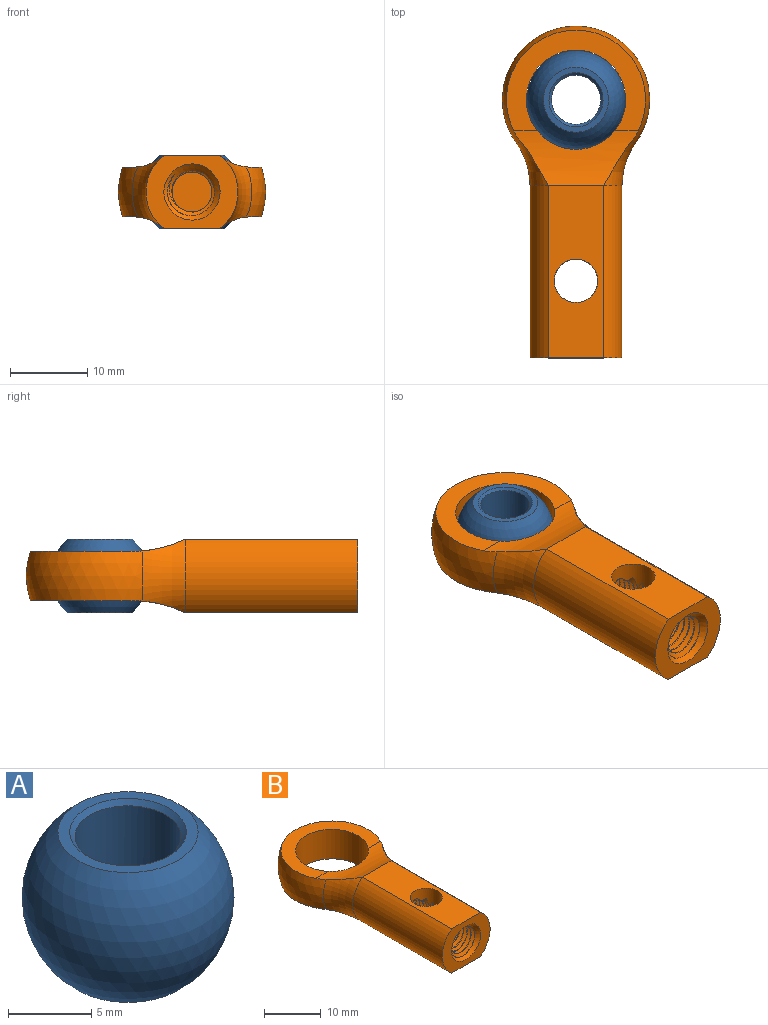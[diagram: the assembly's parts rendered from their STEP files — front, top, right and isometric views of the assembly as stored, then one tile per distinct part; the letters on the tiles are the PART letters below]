
ASSEMBLY  parts=2 mates=1
PART A: 6 faces, bbox 12.7x12.7x9.5 mm
  f0: cone r=3.49mm half-angle=45deg, axis (0,0,1), area 9.4mm2, adj f2,f4
  f1: cone r=3.49mm half-angle=45deg, axis (0,0,-1), area 9.4mm2, adj f2,f5
  f2: cylinder r=3.17mm len=8.89mm, axis (0,0,1), area 177.3mm2, adj f0,f1
  f3: sphere r=6.35mm, area 380mm2, adj f4,f5
  f4: plane 8.4x8.4mm, normal (0,0,1), area 17.1mm2, adj f0,f3
  f5: plane 8.4x8.4mm, normal (0,0,-1), area 17.1mm2, adj f1,f3
PART B: 63 faces, bbox 19.4x43.2x15.5 mm
  f0: cylinder r=3.17mm len=4mm, axis (0,-1,0), area 0.5mm2, adj f1,f2,f62
  f1: bspline ~4.49x1.35mm, area 0mm2, adj f0,f2
  f2: cylinder r=2.81mm len=9.53mm, axis (0,0,1), area 100.4mm2, adj f0,f1,f3,f4,f5,f7,f8,f9
  f3: bspline ~4.49x1.35mm, area 0mm2, adj f2,f4
  f4: cylinder r=3.17mm len=4.23mm, axis (0,-1,0), area 0.5mm2, adj f2,f3,f21
  f5: cylinder r=2.59mm len=5.17mm, axis (0,1,0), area 11.5mm2, adj f2,f6,f15,f17
  f6: plane 6.16x6.13mm, normal (0,-1,0), area 26.2mm2, adj f5,f15,f16,f17
  f7: bspline ~3.51x0.56mm, area 0mm2, adj f2,f8
  f8: cylinder r=3.17mm len=3.64mm, axis (0,-1,0), area 0.4mm2, adj f2,f7,f9
  f9: bspline ~4.49x1.35mm, area 1.9mm2, adj f2,f8,f10
  f10: cylinder r=2.59mm len=2.07mm, axis (0,1,0), area 0.2mm2, adj f2,f9,f11
  f11: bspline ~6.35x3.18mm, area 2.5mm2, adj f2,f10,f12
  f12: cylinder r=3.17mm len=4.92mm, axis (0,-1,0), area 0.6mm2, adj f2,f11,f13
  f13: bspline ~6.35x3.18mm, area 3.5mm2, adj f2,f12,f14
  f14: cylinder r=2.59mm len=4.32mm, axis (0,1,0), area 0.6mm2, adj f2,f13,f15
  f15: bspline ~6.35x6.35mm, area 69.1mm2, adj f2,f5,f6,f14,f16
  f16: cylinder r=3.17mm len=6.35mm, axis (0,-1,0), area 12.2mm2, adj f2,f6,f15,f17
  f17: bspline ~6.35x6.33mm, area 69.3mm2, adj f2,f5,f6,f16,f18
  f18: cylinder r=3.17mm len=5.68mm, axis (0,-1,0), area 0.8mm2, adj f2,f17,f19
  f19: bspline ~6.35x3.18mm, area 3.4mm2, adj f2,f18,f20
  f20: cylinder r=2.59mm len=3.26mm, axis (0,1,0), area 0.4mm2, adj f2,f19,f21
  f21: bspline ~4.49x1.35mm, area 2.6mm2, adj f2,f4,f20
  f22: bspline ~4.49x1.35mm, area 0mm2, adj f2,f23
  f23: cylinder r=3.17mm len=3.2mm, axis (0,-1,0), area 0.4mm2, adj f2,f22,f24
  f24: bspline ~4.49x1.35mm, area 0mm2, adj f2,f23
  f25: bspline ~4.49x1.35mm, area 0mm2, adj f2,f27
  f26: bspline ~2.25x1.35mm, area 0mm2, adj f2,f27
  f27: cylinder r=3.17mm len=3.09mm, axis (0,-1,0), area 0.9mm2, adj f2,f25,f26
  f28: bspline ~3.35x0.5mm, area 0mm2, adj f2,f29
  f29: cylinder r=3.17mm len=3.46mm, axis (0,-1,0), area 0.4mm2, adj f2,f28,f30
  f30: bspline ~4.49x1.35mm, area 1.6mm2, adj f2,f29,f31
  f31: cylinder r=2.59mm len=1.55mm, axis (0,1,0), area 0.2mm2, adj f2,f30,f32
  f32: bspline ~5.42x3.18mm, area 2.2mm2, adj f2,f31,f33
  f33: cylinder r=3.17mm len=4.66mm, axis (0,-1,0), area 0.6mm2, adj f2,f32,f56
  f34: bspline ~7.59x6.35mm, area 89.2mm2, adj f2,f35,f51,f53
  f35: cone r=3.63mm half-angle=45deg, axis (0,-1,0), area 21.4mm2, adj f34,f36,f51,f52,f53
  f36: plane 11.89x9.53mm, normal (0,-1,0), area 58.2mm2, adj f35,f37,f46,f58,f61
  f37: cylinder r=5.94mm len=22.22mm, axis (0,1,0), area 245.5mm2, adj f36,f38,f58,f61
  f38: torus R=15.47mm, axis (0,-1,0), area 52.1mm2, adj f37,f39,f44,f45
  f39: sphere r=9.53mm, area 271.3mm2, adj f38,f40,f42,f43,f44,f45
  f40: plane 17.96x13mm, normal (0,0,1), area 83.8mm2, adj f39,f41,f45
  f41: cylinder r=6.41mm len=12.83mm, axis (0,0,1), area 255.9mm2, adj f40,f42,f44,f45
  f42: plane 17.96x13mm, normal (0,0,-1), area 83.8mm2, adj f39,f41,f44
  f43: torus R=15.47mm, axis (0,-1,0), area 52.1mm2, adj f39,f44,f45,f46
  f44: cylinder r=16.67mm len=16.06mm, axis (1,0,0), area 67.8mm2, adj f38,f39,f41,f42,f43,f61
  f45: cylinder r=16.67mm len=16.06mm, axis (-1,0,0), area 67.8mm2, adj f38,f39,f40,f41,f43,f58
  f46: cylinder r=5.94mm len=22.22mm, axis (0,1,0), area 245.5mm2, adj f36,f43,f58,f61
  f47: cylinder r=2.59mm len=2.85mm, axis (0,1,0), area 0.3mm2, adj f2,f48,f62
  f48: bspline ~6.35x3.18mm, area 3.1mm2, adj f2,f47,f49
  f49: cylinder r=3.17mm len=5.4mm, axis (0,-1,0), area 0.7mm2, adj f2,f48,f50
  f50: bspline ~6.35x3.18mm, area 4.4mm2, adj f2,f49,f51
  f51: cylinder r=2.59mm len=6.47mm, axis (0,1,0), area 17mm2, adj f2,f34,f35,f50,f52
  f52: bspline ~7.03x6.35mm, area 88.8mm2, adj f2,f35,f51,f53
  f53: cylinder r=3.17mm len=7.07mm, axis (0,-1,0), area 17.5mm2, adj f2,f34,f35,f52,f54
  f54: bspline ~6.35x3.18mm, area 4.3mm2, adj f2,f53,f55
  f55: cylinder r=2.59mm len=3.94mm, axis (0,1,0), area 0.5mm2, adj f2,f54,f56
  f56: bspline ~5.42x3.18mm, area 3.2mm2, adj f2,f33,f55
  f57: bspline ~4.49x1.35mm, area 0mm2, adj f2,f60
  f58: plane 22.22x7.11mm, normal (0,0,1), area 133.3mm2, adj f2,f36,f37,f45,f46
  f59: bspline ~4.49x1.35mm, area 0.9mm2, adj f2,f60
  f60: cylinder r=3.17mm len=2.99mm, axis (0,-1,0), area 0.4mm2, adj f2,f57,f59
  f61: plane 22.22x7.11mm, normal (0,0,-1), area 133.3mm2, adj f2,f36,f37,f44,f46
  f62: bspline ~4.49x1.35mm, area 2.4mm2, adj f0,f2,f47
PLACE A t=(0,6.14,-4.76)mm
PLACE B t=(0,6.14,-4.76)mm
MATE ball A.f0 <-> B.f41  axis (0,0,1) through (0,22.01,-4.76)mm
